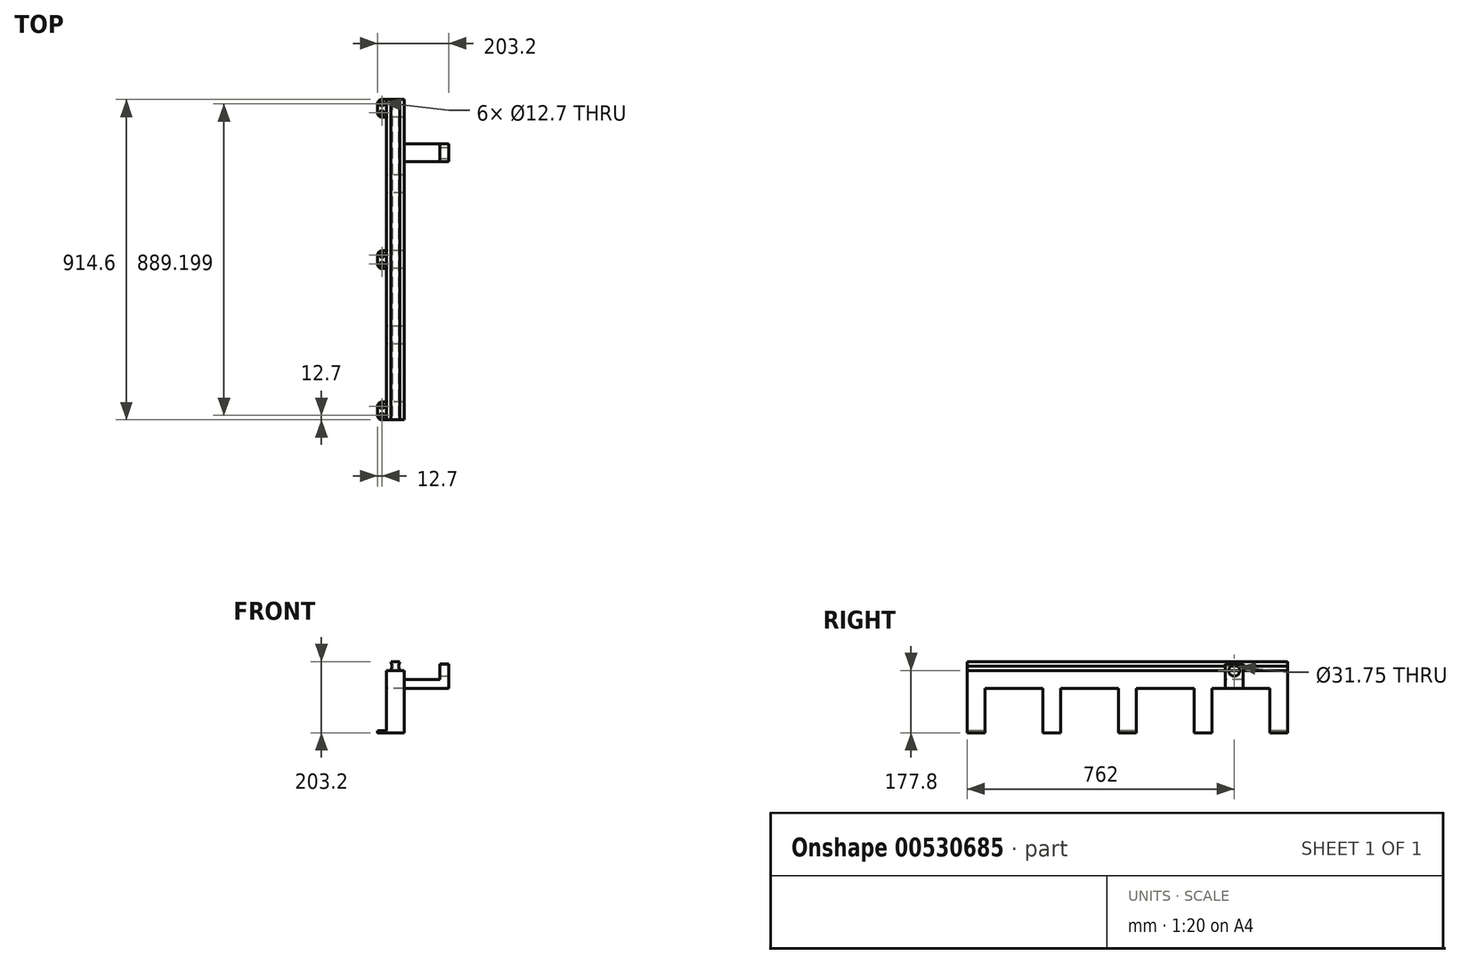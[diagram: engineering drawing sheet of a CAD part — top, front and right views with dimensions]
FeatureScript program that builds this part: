
annotation { "Feature Type Name" : "Feature", "Feature Type Description" : "" }
export const myFeature = defineFeature(function(context is Context, id is Id, definition is map)
    precondition{}
    {
        {
            var Q0;
            Q0=qCreatedBy(makeId("Right.planeOp"),FACE);
            var sketch = newSketch(context, id + "F0", { "sketchPlane" : qUnion([Q0])});
            skLineSegment(sketch, "E0", {"start": v(0, 0) * mm, "end": v(914.4, 0) * mm});
            skLineSegment(sketch, "E1", {"start": v(914.4, 0) * mm, "end": v(914.4, -177.8) * mm});
            skLineSegment(sketch, "E2", {"start": v(914.4, -177.8) * mm, "end": v(863.6, -177.8) * mm});
            skLineSegment(sketch, "E3", {"start": v(863.6, -177.8) * mm, "end": v(863.6, -50.8) * mm});
            skLineSegment(sketch, "E4", {"start": v(863.6, -50.8) * mm, "end": v(698.5, -50.8) * mm});
            skLineSegment(sketch, "E5", {"start": v(698.5, -50.8) * mm, "end": v(698.5, -177.8) * mm});
            skLineSegment(sketch, "E6", {"start": v(698.5, -177.8) * mm, "end": v(647.7, -177.8) * mm});
            skLineSegment(sketch, "E7", {"start": v(647.7, -177.8) * mm, "end": v(647.7, -50.8) * mm});
            skLineSegment(sketch, "E8", {"start": v(647.7, -50.8) * mm, "end": v(482.6, -50.8) * mm});
            skLineSegment(sketch, "E9", {"start": v(482.6, -50.8) * mm, "end": v(482.6, -177.8) * mm});
            skPoint(sketch, "E9.endSnap0", {"position": v(673.1, -177.8) * mm});
            skLineSegment(sketch, "E10", {"start": v(482.6, -177.8) * mm, "end": v(431.8, -177.8) * mm});
            skLineSegment(sketch, "E11", {"start": v(431.8, -177.8) * mm, "end": v(431.8, -50.8) * mm});
            skLineSegment(sketch, "E12", {"start": v(431.8, -50.8) * mm, "end": v(266.7, -50.8) * mm});
            skLineSegment(sketch, "E13", {"start": v(266.7, -50.8) * mm, "end": v(266.7, -177.8) * mm});
            skLineSegment(sketch, "E14", {"start": v(266.7, -177.8) * mm, "end": v(215.9, -177.8) * mm});
            skLineSegment(sketch, "E15", {"start": v(215.9, -177.8) * mm, "end": v(215.9, -50.8) * mm});
            skLineSegment(sketch, "E16", {"start": v(215.9, -50.8) * mm, "end": v(50.8, -50.8) * mm});
            skLineSegment(sketch, "E17", {"start": v(50.8, -50.8) * mm, "end": v(50.8, -177.8) * mm});
            skLineSegment(sketch, "E18", {"start": v(50.8, -177.8) * mm, "end": v(0, -177.8) * mm});
            skLineSegment(sketch, "E19", {"start": v(0, -177.8) * mm, "end": v(0, 0) * mm});
            skSolve(sketch);
        }
        {
            var Q0;
            Q0=makeQuery(id+"F0.imprint","IMPRINT",FACE,{"disambiguationData":[TD([[makeQuery(id+"F0.imprint","IMPRINT",EDGE,{"derivedFrom":sQuery(id+"F0.wireOp",EDGE,"E0")}),-1.0]])]});
            extrude(context, id + "F1", {"entities" : qUnion([Q0]), "depth" : 50.8 * mm, "offsetDistance" : 25.4 * mm});
        }
        {
            var Q0;
            Q0=qCreatedBy(makeId("Front.planeOp"),FACE);
            var sketch = newSketch(context, id + "F2", { "sketchPlane" : qUnion([Q0])});
            skLineSegment(sketch, "E20", {"start": v(0, 0) * mm, "end": v(12.7, 0) * mm});
            skLineSegment(sketch, "E21.bottom", {"start": v(12.7, 0) * mm, "end": v(38.1, 0) * mm});
            skLineSegment(sketch, "E22", {"start": v(12.7, 25.4) * mm, "end": v(38.1, 25.4) * mm});
            skLineSegment(sketch, "E23", {"start": v(12.7, 0) * mm, "end": v(16.63, 12.7) * mm});
            skLineSegment(sketch, "E24", {"start": v(16.63, 12.7) * mm, "end": v(12.7, 25.4) * mm});
            skLineSegment(sketch, "E25", {"start": v(25.4, 25.4) * mm, "end": v(25.4, 0) * mm, "construction": true});
            skLineSegment(sketch, "E26.MirrorCS", {"start": v(34.17, 12.7) * mm, "end": v(38.1, 25.4) * mm});
            skLineSegment(sketch, "E27.MirrorCS", {"start": v(38.1, 0) * mm, "end": v(34.17, 12.7) * mm});
            skSolve(sketch);
        }
        {
            var Q0;
            Q0=makeQuery(id+"F2.imprint","IMPRINT",FACE,{"disambiguationData":[TD([[makeQuery(id+"F2.imprint","IMPRINT",EDGE,{"derivedFrom":sQuery(id+"F2.wireOp",EDGE,"E21.bottom")}),1.0]])]});
            extrude(context, id + "F3", {"entities" : qUnion([Q0]), "oppositeDirection" : true, "depth" : 914.4 * mm, "offsetDistance" : 25.4 * mm});
        }
        {
            var Q0;
            Q0=qCreatedBy(makeId("Front.planeOp"),FACE);
            cPlane(context, id + "F4", {"entities" : qUnion([Q0]), "cplaneType" : CPlaneType.OFFSET, "offset" : 736.6 * mm, "oppositeDirection" : true, "width" : 152.4 * mm, "height" : 152.4 * mm});
        }
        {
            var Q0;
            Q0=qCreatedBy(id+"F4.planeOp",FACE);
            var sketch = newSketch(context, id + "F5", { "sketchPlane" : qUnion([Q0])});
            skLineSegment(sketch, "E28", {"start": v(50.8, -50.8) * mm, "end": v(177.8, -50.8) * mm});
            skLineSegment(sketch, "E29", {"start": v(177.8, -50.8) * mm, "end": v(177.8, 19.05) * mm});
            skLineSegment(sketch, "E30", {"start": v(177.8, 19.05) * mm, "end": v(152.4, 19.05) * mm});
            skLineSegment(sketch, "E31", {"start": v(152.4, 19.05) * mm, "end": v(152.4, -25.4) * mm});
            skLineSegment(sketch, "E32", {"start": v(152.4, -25.4) * mm, "end": v(50.8, -25.4) * mm});
            skLineSegment(sketch, "E33", {"start": v(50.8, -25.4) * mm, "end": v(50.8, -50.8) * mm});
            skSolve(sketch);
        }
        {
            var Q0;
            Q0=qSketchRegion(id+"F5",true);
            extrude(context, id + "F6", {"entities" : qUnion([Q0]), "operationType" : NewBodyOperationType.ADD, "oppositeDirection" : true, "depth" : 50.8 * mm, "offsetDistance" : 25.4 * mm});
        }
        {
            var Q0;
            Q0=makeQuery(id+"F6.opExtrude","SWEPT_FACE",FACE,{"disambiguationData":[OSD([sQuery(id+"F5.wireOp",EDGE,"E29")])]});
            cPlane(context, id + "F7", {"entities" : qUnion([Q0]), "cplaneType" : CPlaneType.OFFSET, "offset" : 0 * mm, "width" : 152.4 * mm, "height" : 152.4 * mm});
        }
        {
            var Q0;
            Q0=qCreatedBy(id+"F7.planeOp",FACE);
            var sketch = newSketch(context, id + "F8", { "sketchPlane" : qUnion([Q0])});
            skCircle(sketch, "E34", {"center": v(762, 0) * mm, "radius": 15.88 * mm});
            skSolve(sketch);
        }
        {
            var Q0;
            Q0=qSketchRegion(id+"F8",true);
            extrude(context, id + "F9", {"entities" : qUnion([Q0]), "operationType" : NewBodyOperationType.REMOVE, "oppositeDirection" : true, "depth" : 25.4 * mm, "offsetDistance" : 25.4 * mm});
        }
        {
            var Q0;
            Q0=makeQuery(id+"F1.opExtrude","SWEPT_FACE",FACE,{"disambiguationData":[OSD([sQuery(id+"F0.wireOp",EDGE,"E18")])]});
            cPlane(context, id + "F10", {"entities" : qUnion([Q0]), "cplaneType" : CPlaneType.OFFSET, "offset" : 0 * mm, "width" : 152.4 * mm, "height" : 152.4 * mm});
        }
        {
            var Q0;
            Q0=qCreatedBy(id+"F10.planeOp",FACE);
            var sketch = newSketch(context, id + "F11", { "sketchPlane" : qUnion([Q0])});
            skLineSegment(sketch, "E35", {"start": v(0, 0) * mm, "end": v(0, -51.1) * mm});
            skLineSegment(sketch, "E36", {"start": v(0, -51.1) * mm, "end": v(-12.7, -51.1) * mm});
            skLineSegment(sketch, "E37", {"start": v(-25.4, -38.4) * mm, "end": v(-25.4, -12.7) * mm});
            skLineSegment(sketch, "E38", {"start": v(-12.7, 0) * mm, "end": v(0, 0) * mm});
            skPoint(sketch, "E39.visualSharp", {"position": v(-25.4, 0) * mm});
            skArc(sketch, "E39.filletArc", {"start": v(-12.7, 0) * mm, "mid": v(-21.68, -3.72) * mm, "end": v(-25.4, -12.7) * mm});
            skPoint(sketch, "E40.visualSharp", {"position": v(-25.4, -51.1) * mm});
            skArc(sketch, "E40.filletArc", {"start": v(-25.4, -38.4) * mm, "mid": v(-21.68, -47.38) * mm, "end": v(-12.7, -51.1) * mm});
            skCircle(sketch, "E41", {"center": v(-12.7, -38.4) * mm, "radius": 6.35 * mm});
            skCircle(sketch, "E42", {"center": v(-12.7, -12.7) * mm, "radius": 6.35 * mm});
            skLineSegment(sketch, "E43", {"start": v(0, -863.8) * mm, "end": v(0, -914.6) * mm});
            skLineSegment(sketch, "E44", {"start": v(0, -914.6) * mm, "end": v(-12.7, -914.6) * mm});
            skLineSegment(sketch, "E45", {"start": v(-25.4, -901.9) * mm, "end": v(-25.4, -876.5) * mm});
            skLineSegment(sketch, "E46", {"start": v(-12.7, -863.8) * mm, "end": v(0, -863.8) * mm});
            skPoint(sketch, "E47.visualSharp", {"position": v(-25.4, -863.8) * mm});
            skArc(sketch, "E47.filletArc", {"start": v(-12.7, -863.8) * mm, "mid": v(-21.68, -867.52) * mm, "end": v(-25.4, -876.5) * mm});
            skPoint(sketch, "E48.visualSharp", {"position": v(-25.4, -914.6) * mm});
            skArc(sketch, "E48.filletArc", {"start": v(-25.4, -901.9) * mm, "mid": v(-21.68, -910.88) * mm, "end": v(-12.7, -914.6) * mm});
            skCircle(sketch, "E49", {"center": v(-12.7, -876.5) * mm, "radius": 6.35 * mm});
            skCircle(sketch, "E50", {"center": v(-12.7, -901.9) * mm, "radius": 6.35 * mm});
            skLineSegment(sketch, "E51", {"start": v(0, -431.82) * mm, "end": v(0, -482.62) * mm});
            skLineSegment(sketch, "E52", {"start": v(0, -482.62) * mm, "end": v(-12.7, -482.62) * mm});
            skLineSegment(sketch, "E53", {"start": v(-25.4, -469.92) * mm, "end": v(-25.4, -444.52) * mm});
            skLineSegment(sketch, "E54", {"start": v(-12.7, -431.82) * mm, "end": v(0, -431.82) * mm});
            skPoint(sketch, "E55.visualSharp", {"position": v(-25.4, -431.82) * mm});
            skArc(sketch, "E55.filletArc", {"start": v(-12.7, -431.82) * mm, "mid": v(-21.68, -435.54) * mm, "end": v(-25.4, -444.52) * mm});
            skPoint(sketch, "E56.visualSharp", {"position": v(-25.4, -482.62) * mm});
            skArc(sketch, "E56.filletArc", {"start": v(-25.4, -469.92) * mm, "mid": v(-21.68, -478.9) * mm, "end": v(-12.7, -482.62) * mm});
            skCircle(sketch, "E57", {"center": v(-12.7, -444.52) * mm, "radius": 6.35 * mm});
            skCircle(sketch, "E58", {"center": v(-12.7, -469.92) * mm, "radius": 6.35 * mm});
            skSolve(sketch);
        }
        {
            var Q0;
            Q0=qSketchRegion(id+"F11",true);
            extrude(context, id + "F12", {"entities" : qUnion([Q0]), "operationType" : NewBodyOperationType.ADD, "oppositeDirection" : true, "depth" : 6.35 * mm, "offsetDistance" : 25.4 * mm});
        }
    });
